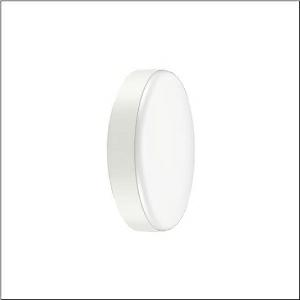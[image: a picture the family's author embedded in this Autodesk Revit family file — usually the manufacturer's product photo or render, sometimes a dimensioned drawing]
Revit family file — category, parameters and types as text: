
# Revit family: round_31_51wc10mb44a
name_source: partatom
category: Lighting Fixtures
units: mm (PartAtom-declared; Revit-internal decimal feet)

## family parameters
Cut with Voids When Loaded = No
Host = Face
Light Source = No
Part Type = Normal
Room Calculation Point = No
Round Connector Dimension = Use Diameter
Shared = No

## types (1)
- --- (1 x LED, 4400 lm, 34 W, 4000K)
    Apparent Load = 34 VA
    CIE Flux Codes = 44 75 94 94 100
    Color Rendering = 80
    Color Temperature = 4000K
    Default Elevation = 1800 mm
    Description = Round 31, wall and ceiling luminaire, primary optical cover: cover, of PC, opal, light emission: direct distribution, primary light characteristic: symmetric, installation type: surface-mounted, LED, rated luminous flux: 4.400lm, luminous efficacy: 129lm/W, light colour: 840, colour temperature: 4000K, control gear: ON/OFF Multilumen, with terminal, 3-pole, max. 2.5mm², mains connection: 220..240V, AC, 50/60Hz, rated input power: 34W, luminaire housing, of PC, traffic white (RAL 9016), diameter: 480mm, protection rating (complete): IP65, insulation class (complete): insulation class II (safety insulation), certification: CE, impact resistance: IK10, permissible operating ambient temperature: -20..+40°C, permissible storage temperature: -20..+60°C, packaging unit: 1 piece
    Height = 97 mm
    Lamp = 1 x LED
    Lamp Light Flux = 4400 lm
    Lamp Power = 34 W
    Lamp count = 1
    Length = 480 mm
    Luminous efficacy = 129 lm/W
    Manufacturer = Siteco
    ModVariant = No
    Model = 51WC10MB44A
    Mounting Place = Ceiling
    Mounting Type = Surface mounted
    Number of Poles = 1
    OnlyDefault = Yes
    Power Factor = 1
    Product Name = Round 31
    Product group = wall and ceiling luminaire
    ProductGroupID = 304
    Protection Class = Protection class II
    Protection Degree = IP 65
    RLX_Detail_Level = 1
    RLX_Emergency_Light_Flux = 0 lm
    RLX_Emergency_Type = 0
    RLX_Emergency_Type_DB = No
    RlxData = <blob elided: 56377 chars, md5=a0af1590>
    Socket = socket
    Standby Power = 0 W
    System Light Flux = 4400 lm
    System Power = 34 W
    Type Comments = factory setting: luminous flux: 100 % | (ON | ON)
    Type Image = l_1007188.jpg
    URL = http://relux.com
    VarID = @adj_150848
    Voltage = 0 V
    Weight = 0.00 kg
    Width = 0 mm  [stored 0 ft]

note: [stored X ft] marks values corroborated as IEEE doubles in the binary element streams (Revit-internal decimal feet)

## geometry (parser evidence)
native form markers: Blend x4, Sweep x13
no freeform markers — native parametric forms only
